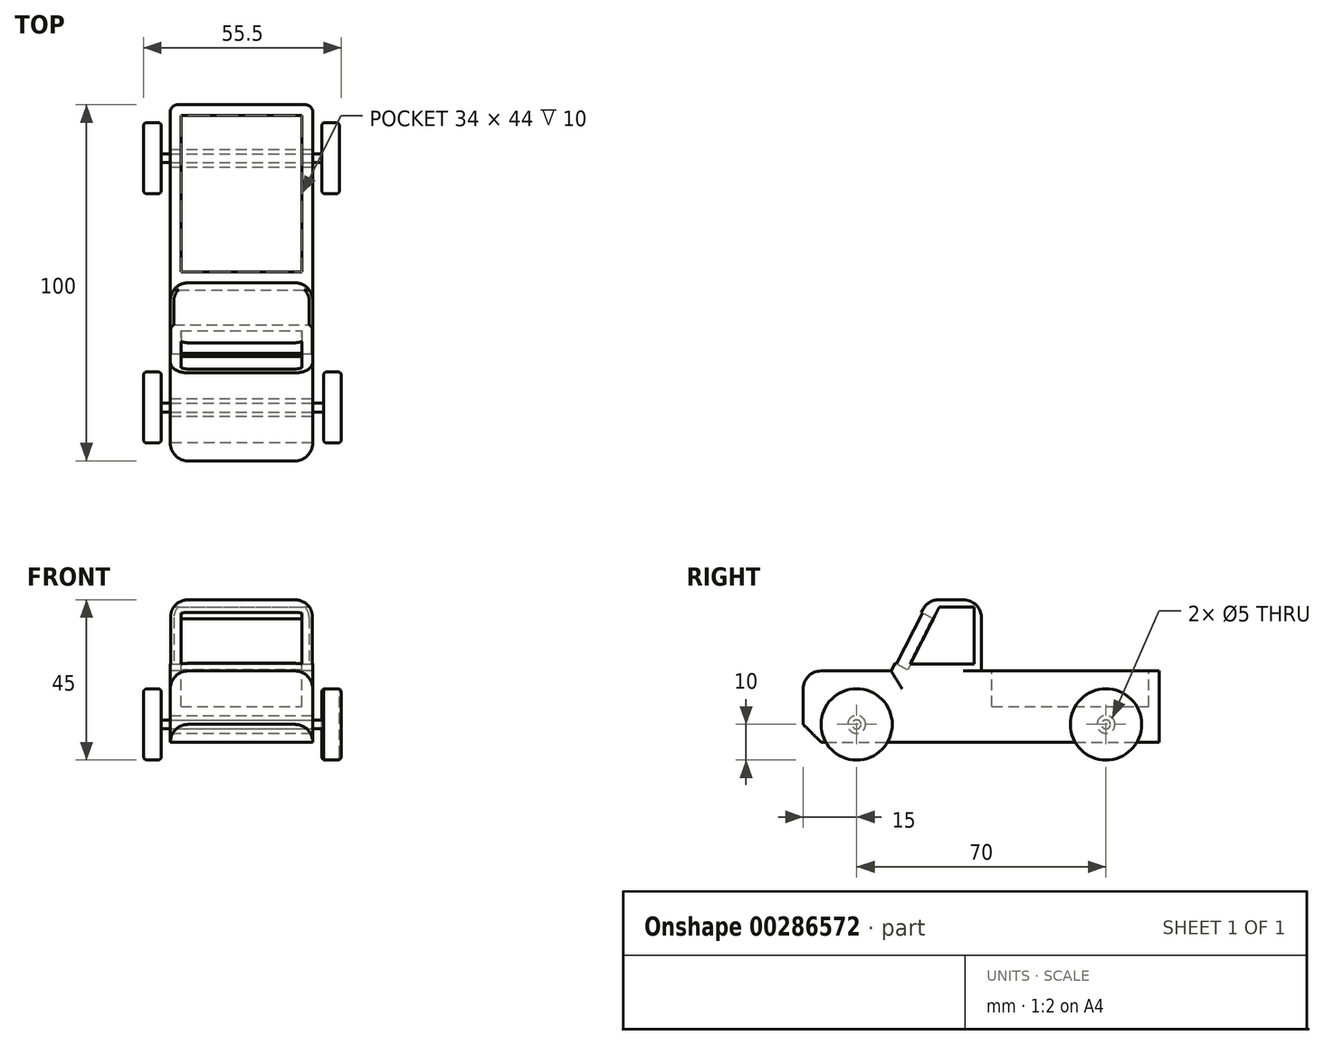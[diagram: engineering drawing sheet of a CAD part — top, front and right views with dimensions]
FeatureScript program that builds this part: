
annotation { "Feature Type Name" : "Feature", "Feature Type Description" : "" }
export const myFeature = defineFeature(function(context is Context, id is Id, definition is map)
    precondition{}
    {
        {
            var Q0;
            Q0=qCreatedBy(makeId("Right.planeOp"),FACE);
            var sketch = newSketch(context, id + "F0", { "sketchPlane" : qUnion([Q0])});
            skLineSegment(sketch, "E0.top", {"start": v(-50, -10) * mm, "end": v(50, -10) * mm});
            skLineSegment(sketch, "E0.left", {"start": v(-50, 10) * mm, "end": v(-50, -10) * mm});
            skLineSegment(sketch, "E0.right", {"start": v(50, 10) * mm, "end": v(50, -10) * mm});
            skPoint(sketch, "E0.middle", {"position": v(0, 0) * mm});
            skLineSegment(sketch, "E1", {"start": v(0, 10) * mm, "end": v(0, 30) * mm});
            skPoint(sketch, "E1.endSnap0", {"position": v(0, 10) * mm});
            skLineSegment(sketch, "E2", {"start": v(0, 30) * mm, "end": v(-15, 30) * mm});
            skPoint(sketch, "E3", {"position": v(-25.3, 10) * mm});
            skLineSegment(sketch, "E4", {"start": v(-15, 30) * mm, "end": v(-25.3, 10) * mm});
            skLineSegment(sketch, "E5", {"start": v(-50, 10) * mm, "end": v(-25.3, 10) * mm});
            skLineSegment(sketch, "E6", {"start": v(0, 10) * mm, "end": v(50, 10) * mm});
            skSolve(sketch);
        }
        {
            var Q0;
            Q0 = qSketchRegion(id + "F0", true);
            extrude(context, id + "F1", {"entities" : qUnion([Q0]), "endBound" : BoundingType.SYMMETRIC, "depth" : 40 * mm});
        }
        {
            var Q0;
            Q0=makeQuery(id+"F1.opExtrude","CAP_FACE",FACE,{"disambiguationData":[OSD([sQuery(id+"F0.wireOp",EDGE,"E0.bottom"),sQuery(id+"F0.wireOp",EDGE,"E0.top"),sQuery(id+"F0.wireOp",EDGE,"E0.left"),sQuery(id+"F0.wireOp",EDGE,"E0.right")])],"isStart":false});
            var sketch = newSketch(context, id + "F2", { "sketchPlane" : qUnion([Q0])});
            skCircle(sketch, "E7", {"center": v(-35, -5) * mm, "radius": 2.5 * mm});
            skCircle(sketch, "E8", {"center": v(165.27, -6.7) * mm, "radius": 18.84 * mm});
            skCircle(sketch, "E9", {"center": v(-35, -5) * mm, "radius": 1.25 * mm});
            skSolve(sketch);
        }
        {
            var Q0;
            Q0 = qSketchRegion(id + "F2", true);
            extrude(context, id + "F3", {"entities" : qUnion([Q0]), "operationType" : NewBodyOperationType.REMOVE, "endBound" : BoundingType.THROUGH_ALL, "oppositeDirection" : true, "depth" : 25 * mm});
        }
        {
            var Q0;
            Q0=makeQuery(id+"F1.opExtrude","CAP_FACE",FACE,{"disambiguationData":[OSD([sQuery(id+"F0.wireOp",EDGE,"E0.bottom"),sQuery(id+"F0.wireOp",EDGE,"E0.top"),sQuery(id+"F0.wireOp",EDGE,"E0.left"),sQuery(id+"F0.wireOp",EDGE,"E0.right")])],"isStart":false});
            var sketch = newSketch(context, id + "F4", { "sketchPlane" : qUnion([Q0])});
            skCircle(sketch, "E10", {"center": v(35, -5) * mm, "radius": 2.5 * mm});
            skCircle(sketch, "E11", {"center": v(35, -5) * mm, "radius": 1.25 * mm});
            skSolve(sketch);
        }
        {
            var Q0;
            Q0 = qSketchRegion(id + "F4", true);
            extrude(context, id + "F5", {"entities" : qUnion([Q0]), "operationType" : NewBodyOperationType.REMOVE, "endBound" : BoundingType.THROUGH_ALL, "oppositeDirection" : true, "depth" : 25 * mm});
        }
        {
            var Q0;
            Q0=makeQuery(id+"F1.opExtrude","SWEPT_FACE",FACE,{"disambiguationData":[OSD([sQuery(id+"F0.wireOp",EDGE,"E6")])]});
            var sketch = newSketch(context, id + "F6", { "sketchPlane" : qUnion([Q0])});
            skLineSegment(sketch, "E12.bottom", {"start": v(-17, 3) * mm, "end": v(17, 3) * mm});
            skLineSegment(sketch, "E12.top", {"start": v(-17, 47) * mm, "end": v(17, 47) * mm});
            skLineSegment(sketch, "E12.left", {"start": v(-17, 3) * mm, "end": v(-17, 47) * mm});
            skLineSegment(sketch, "E12.right", {"start": v(17, 3) * mm, "end": v(17, 47) * mm});
            skPoint(sketch, "E12.middle", {"position": v(0, 25) * mm});
            skSolve(sketch);
        }
        {
            var Q0;
            Q0=makeQuery(id+"F6.imprint","IMPRINT",FACE,{"disambiguationData":[TD([[makeQuery(id+"F6.imprint","IMPRINT",EDGE,{"derivedFrom":sQuery(id+"F6.wireOp",EDGE,"E12.bottom")}),1.0]])]});
            extrude(context, id + "F7", {"entities" : qUnion([Q0]), "operationType" : NewBodyOperationType.REMOVE, "oppositeDirection" : true, "depth" : 10 * mm});
        }
        {
            var Q0;
            Q0=makeQuery(id+"F3.boolean.opBoolean","SPLIT",FACE,{"disambiguationData":[TD([makeQuery(id+"F3.opExtrude","SWEPT_FACE",FACE,{"disambiguationData":[OSD([sQuery(id+"F2.wireOp",EDGE,"E9")])]})])],"derivedFrom":makeQuery(id+"F1.opExtrude","CAP_FACE",FACE,{"disambiguationData":[OSD([sQuery(id+"F0.wireOp",EDGE,"E0.top"),sQuery(id+"F0.wireOp",EDGE,"E0.left"),sQuery(id+"F0.wireOp",EDGE,"E0.right"),sQuery(id+"F0.wireOp",EDGE,"E1"),sQuery(id+"F0.wireOp",EDGE,"E2"),sQuery(id+"F0.wireOp",EDGE,"E4"),sQuery(id+"F0.wireOp",EDGE,"E5"),sQuery(id+"F0.wireOp",EDGE,"E6")])],"isStart":false})});
            extrude(context, id + "F8", {"entities" : qUnion([Q0]), "operationType" : NewBodyOperationType.ADD, "oppositeDirection" : true, "depth" : 42.5 * mm});
        }
        {
            var Q0;
            {var subQ0=sQuery(id+"F0.wireOp",EDGE,"E0.right");var subQ1=sQuery(id+"F0.wireOp",EDGE,"E0.left");var subQ2=sQuery(id+"F0.wireOp",EDGE,"E1");var subQ3=sQuery(id+"F0.wireOp",EDGE,"E0.top");var subQ4=sQuery(id+"F0.wireOp",EDGE,"E2");var subQ5=sQuery(id+"F0.wireOp",EDGE,"E4");var subQ6=sQuery(id+"F0.wireOp",EDGE,"E5");var subQ7=sQuery(id+"F0.wireOp",EDGE,"E6");Q0=makeQuery(id+"F5.boolean.opBoolean","SPLIT",FACE,{"disambiguationData":[TD([makeQuery(id+"F5.opExtrude","SWEPT_FACE",FACE,{"disambiguationData":[OSD([sQuery(id+"F4.wireOp",EDGE,"E11")])]})])],"derivedFrom":makeQuery(id+"F3.boolean.opBoolean","SPLIT",FACE,{"disambiguationData":[TD([makeQuery(id+"F1.opExtrude","SWEPT_FACE",FACE,{"disambiguationData":[OSD([subQ3])]})])],"derivedFrom":makeQuery(id+"F1.opExtrude","CAP_FACE",FACE,{"disambiguationData":[OSD([subQ3,subQ1,subQ0,subQ2,subQ4,subQ5,subQ6,subQ7])],"isStart":false})})});}
            extrude(context, id + "F9", {"entities" : qUnion([Q0]), "operationType" : NewBodyOperationType.ADD, "oppositeDirection" : true, "depth" : 42.5 * mm});
        }
        {
            var Q0;
            Q0=makeQuery(id+"F3.boolean.opBoolean","SPLIT",FACE,{"disambiguationData":[TD([makeQuery(id+"F3.opExtrude","SWEPT_FACE",FACE,{"disambiguationData":[OSD([sQuery(id+"F2.wireOp",EDGE,"E9")])]})])],"derivedFrom":makeQuery(id+"F1.opExtrude","CAP_FACE",FACE,{"disambiguationData":[OSD([sQuery(id+"F0.wireOp",EDGE,"E0.top"),sQuery(id+"F0.wireOp",EDGE,"E0.left"),sQuery(id+"F0.wireOp",EDGE,"E0.right"),sQuery(id+"F0.wireOp",EDGE,"E1"),sQuery(id+"F0.wireOp",EDGE,"E2"),sQuery(id+"F0.wireOp",EDGE,"E4"),sQuery(id+"F0.wireOp",EDGE,"E5"),sQuery(id+"F0.wireOp",EDGE,"E6")])],"isStart":false})});
            extrude(context, id + "F10", {"entities" : qUnion([Q0]), "operationType" : NewBodyOperationType.ADD, "depth" : 3 * mm});
        }
        {
            var Q0;
            {var subQ0=sQuery(id+"F0.wireOp",EDGE,"E0.right");var subQ1=sQuery(id+"F0.wireOp",EDGE,"E0.left");var subQ2=sQuery(id+"F0.wireOp",EDGE,"E1");var subQ3=sQuery(id+"F0.wireOp",EDGE,"E0.top");var subQ4=sQuery(id+"F0.wireOp",EDGE,"E2");var subQ5=sQuery(id+"F0.wireOp",EDGE,"E4");var subQ6=sQuery(id+"F0.wireOp",EDGE,"E5");var subQ7=sQuery(id+"F0.wireOp",EDGE,"E6");Q0=makeQuery(id+"F5.boolean.opBoolean","SPLIT",FACE,{"disambiguationData":[TD([makeQuery(id+"F5.opExtrude","SWEPT_FACE",FACE,{"disambiguationData":[OSD([sQuery(id+"F4.wireOp",EDGE,"E11")])]})])],"derivedFrom":makeQuery(id+"F3.boolean.opBoolean","SPLIT",FACE,{"disambiguationData":[TD([makeQuery(id+"F1.opExtrude","SWEPT_FACE",FACE,{"disambiguationData":[OSD([subQ3])]})])],"derivedFrom":makeQuery(id+"F1.opExtrude","CAP_FACE",FACE,{"disambiguationData":[OSD([subQ3,subQ1,subQ0,subQ2,subQ4,subQ5,subQ6,subQ7])],"isStart":false})})});}
            extrude(context, id + "F11", {"entities" : qUnion([Q0]), "operationType" : NewBodyOperationType.ADD, "depth" : 2.5 * mm});
        }
        {
            var Q0;
            Q0=makeQuery(id+"F10.opExtrude","CAP_FACE",FACE,{"disambiguationData":[OSD([sQuery(id+"F0.wireOp",EDGE,"E0.top"),sQuery(id+"F0.wireOp",EDGE,"E0.left"),sQuery(id+"F0.wireOp",EDGE,"E0.right"),sQuery(id+"F0.wireOp",EDGE,"E1"),sQuery(id+"F0.wireOp",EDGE,"E2"),sQuery(id+"F0.wireOp",EDGE,"E4"),sQuery(id+"F0.wireOp",EDGE,"E5"),sQuery(id+"F0.wireOp",EDGE,"E6")])],"isStart":false});
            var sketch = newSketch(context, id + "F12", { "sketchPlane" : qUnion([Q0])});
            skCircle(sketch, "E13", {"center": v(-35, -5) * mm, "radius": 10 * mm});
            skSolve(sketch);
        }
        {
            var Q0;
            Q0=makeQuery(id+"F12.imprint","IMPRINT",FACE,{"disambiguationData":[TD([[makeQuery(id+"F12.imprint","IMPRINT",EDGE,{"derivedFrom":sQuery(id+"F12.wireOp",EDGE,"E13")}),1.0]])]});
            extrude(context, id + "F13", {"entities" : qUnion([Q0]), "operationType" : NewBodyOperationType.ADD, "depth" : 5 * mm});
        }
        {
            var Q0;
            Q0=makeQuery(id+"F11.opExtrude","CAP_FACE",FACE,{"disambiguationData":[OSD([sQuery(id+"F0.wireOp",EDGE,"E0.top"),sQuery(id+"F0.wireOp",EDGE,"E0.left"),sQuery(id+"F0.wireOp",EDGE,"E0.right"),sQuery(id+"F0.wireOp",EDGE,"E1"),sQuery(id+"F0.wireOp",EDGE,"E2"),sQuery(id+"F0.wireOp",EDGE,"E4"),sQuery(id+"F0.wireOp",EDGE,"E5"),sQuery(id+"F0.wireOp",EDGE,"E6")])],"isStart":false});
            var sketch = newSketch(context, id + "F14", { "sketchPlane" : qUnion([Q0])});
            skCircle(sketch, "E14", {"center": v(35, -5) * mm, "radius": 10 * mm});
            skSolve(sketch);
        }
        {
            var Q0;
            Q0 = qSketchRegion(id + "F14", true);
            extrude(context, id + "F15", {"entities" : qUnion([Q0]), "operationType" : NewBodyOperationType.ADD, "depth" : 5 * mm});
        }
        {
            var Q0;
            Q0=makeQuery(id+"F13.opExtrude","SWEPT_BODY",BODY,{"disambiguationData":[OSD([sQuery(id+"F2.wireOp",EDGE,"E9"),sQuery(id+"F12.wireOp",EDGE,"E13")])]});
            deleteBodies(context, id + "F16", {"entities" : qUnion([Q0])});
        }
        {
            var Q0;
            Q0=makeQuery(id+"F10.opExtrude","CAP_FACE",FACE,{"disambiguationData":[OSD([sQuery(id+"F0.wireOp",EDGE,"E0.top"),sQuery(id+"F0.wireOp",EDGE,"E0.left"),sQuery(id+"F0.wireOp",EDGE,"E0.right"),sQuery(id+"F0.wireOp",EDGE,"E1"),sQuery(id+"F0.wireOp",EDGE,"E2"),sQuery(id+"F0.wireOp",EDGE,"E4"),sQuery(id+"F0.wireOp",EDGE,"E5"),sQuery(id+"F0.wireOp",EDGE,"E6")])],"isStart":false});
            var sketch = newSketch(context, id + "F17", { "sketchPlane" : qUnion([Q0])});
            skCircle(sketch, "E15", {"center": v(-35, -5) * mm, "radius": 10 * mm});
            skSolve(sketch);
        }
        {
            var Q0;
            Q0 = qSketchRegion(id + "F17", true);
            extrude(context, id + "F18", {"entities" : qUnion([Q0]), "operationType" : NewBodyOperationType.ADD, "depth" : 5 * mm});
        }
        {
            var Q0;
            Q0=makeQuery(id+"F9.opExtrude","CAP_FACE",FACE,{"disambiguationData":[OSD([sQuery(id+"F0.wireOp",EDGE,"E0.top"),sQuery(id+"F0.wireOp",EDGE,"E0.left"),sQuery(id+"F0.wireOp",EDGE,"E0.right"),sQuery(id+"F0.wireOp",EDGE,"E1"),sQuery(id+"F0.wireOp",EDGE,"E2"),sQuery(id+"F0.wireOp",EDGE,"E4"),sQuery(id+"F0.wireOp",EDGE,"E5"),sQuery(id+"F0.wireOp",EDGE,"E6")])],"isStart":false});
            var sketch = newSketch(context, id + "F19", { "sketchPlane" : qUnion([Q0])});
            skCircle(sketch, "E16", {"center": v(-35, -5) * mm, "radius": 10 * mm});
            skSolve(sketch);
        }
        {
            var Q0;
            Q0 = qSketchRegion(id + "F19", true);
            extrude(context, id + "F20", {"entities" : qUnion([Q0]), "operationType" : NewBodyOperationType.ADD, "depth" : 5 * mm});
        }
        {
            var Q0;
            Q0=makeQuery(id+"F8.opExtrude","CAP_FACE",FACE,{"disambiguationData":[OSD([sQuery(id+"F0.wireOp",EDGE,"E0.top"),sQuery(id+"F0.wireOp",EDGE,"E0.left"),sQuery(id+"F0.wireOp",EDGE,"E0.right"),sQuery(id+"F0.wireOp",EDGE,"E1"),sQuery(id+"F0.wireOp",EDGE,"E2"),sQuery(id+"F0.wireOp",EDGE,"E4"),sQuery(id+"F0.wireOp",EDGE,"E5"),sQuery(id+"F0.wireOp",EDGE,"E6")])],"isStart":false});
            var sketch = newSketch(context, id + "F21", { "sketchPlane" : qUnion([Q0])});
            skCircle(sketch, "E17", {"center": v(35, -5) * mm, "radius": 10 * mm});
            skSolve(sketch);
        }
        {
            var Q0;
            Q0 = qSketchRegion(id + "F21", true);
            extrude(context, id + "F22", {"entities" : qUnion([Q0]), "operationType" : NewBodyOperationType.ADD, "depth" : 5 * mm});
        }
        {
            var Q0;
            Q0=makeQuery(id+"F1.opExtrude","SWEPT_FACE",FACE,{"disambiguationData":[OSD([sQuery(id+"F0.wireOp",EDGE,"E4")])]});
            var sketch = newSketch(context, id + "F23", { "sketchPlane" : qUnion([Q0])});
            skLineSegment(sketch, "E18.bottom", {"start": v(17, 15.8) * mm, "end": v(-17, 15.8) * mm});
            skLineSegment(sketch, "E18.top", {"start": v(17, -0.3) * mm, "end": v(-17, -0.3) * mm});
            skLineSegment(sketch, "E18.left", {"start": v(17, 15.8) * mm, "end": v(17, -0.3) * mm});
            skLineSegment(sketch, "E18.right", {"start": v(-17, 15.8) * mm, "end": v(-17, -0.3) * mm});
            skPoint(sketch, "E18.middle", {"position": v(0, 7.75) * mm});
            skSolve(sketch);
        }
        {
            var Q0;
            Q0 = qSketchRegion(id + "F23", true);
            extrude(context, id + "F24", {"entities" : qUnion([Q0]), "operationType" : NewBodyOperationType.REMOVE, "oppositeDirection" : true, "depth" : 4 * mm});
        }
        {
            var Q0;
            {var subQ0=sQuery(id+"F0.wireOp",EDGE,"E0.right");var subQ2=sQuery(id+"F0.wireOp",EDGE,"E0.left");var subQ4=sQuery(id+"F0.wireOp",EDGE,"E1");var subQ7=sQuery(id+"F0.wireOp",EDGE,"E0.top");var subQ8=makeQuery(id+"F1.opExtrude","SWEPT_FACE",FACE,{"disambiguationData":[OSD([subQ7])]});var subQ9=sQuery(id+"F0.wireOp",EDGE,"E2");var subQ11=sQuery(id+"F0.wireOp",EDGE,"E4");var subQ13=sQuery(id+"F0.wireOp",EDGE,"E5");var subQ15=sQuery(id+"F0.wireOp",EDGE,"E6");Q0=makeQuery(id+"F5.boolean.opBoolean","SPLIT",FACE,{"disambiguationData":[TD([subQ8])],"derivedFrom":makeQuery(id+"F3.boolean.opBoolean","SPLIT",FACE,{"disambiguationData":[TD([subQ8])],"derivedFrom":makeQuery(id+"F1.opExtrude","CAP_FACE",FACE,{"disambiguationData":[OSD([subQ7,subQ2,subQ0,subQ4,subQ9,subQ11,subQ13,subQ15])],"isStart":false})})});}
            var sketch = newSketch(context, id + "F25", { "sketchPlane" : qUnion([Q0])});
            skLineSegment(sketch, "E19", {"start": v(-19.96, 12) * mm, "end": v(-2, 12) * mm});
            skLineSegment(sketch, "E20", {"start": v(-2, 12) * mm, "end": v(-2, 28) * mm});
            skLineSegment(sketch, "E21", {"start": v(-2, 28) * mm, "end": v(-11.78, 28) * mm});
            skLineSegment(sketch, "E22", {"start": v(-11.78, 28) * mm, "end": v(-19.96, 12) * mm});
            skSolve(sketch);
        }
        {
            var Q0;
            Q0 = qSketchRegion(id + "F25", true);
            extrude(context, id + "F26", {"entities" : qUnion([Q0]), "operationType" : NewBodyOperationType.REMOVE, "endBound" : BoundingType.THROUGH_ALL, "oppositeDirection" : true, "depth" : 25 * mm});
        }
        {
            var Q0;
            Q0=makeQuery(id+"F1.opExtrude","SWEPT_EDGE",EDGE,{"disambiguationData":[OSD([sQuery(id+"F0.wireOp",EDGE,"E0.left"),sQuery(id+"F0.wireOp",EDGE,"E5")])]});
            fillet(context, id + "F27", {"entities" : qUnion([Q0]), "radius" : 5 * mm, "tangentPropagation" : true, "allowEdgeOverflow" : false});
        }
        {
            var Q0;
            Q0=makeQuery(id+"F1.opExtrude","SWEPT_EDGE",EDGE,{"disambiguationData":[OSD([sQuery(id+"F0.wireOp",EDGE,"E2"),sQuery(id+"F0.wireOp",EDGE,"E4")])]});
            fillet(context, id + "F28", {"entities" : qUnion([Q0]), "radius" : 5 * mm, "tangentPropagation" : true, "allowEdgeOverflow" : false});
        }
        {
            var Q0;
            Q0=makeQuery(id+"F1.opExtrude","SWEPT_EDGE",EDGE,{"disambiguationData":[OSD([sQuery(id+"F0.wireOp",EDGE,"E1"),sQuery(id+"F0.wireOp",EDGE,"E2")])]});
            fillet(context, id + "F29", {"entities" : qUnion([Q0]), "radius" : 5 * mm, "tangentPropagation" : true, "allowEdgeOverflow" : false});
        }
        {
            var Q0;
            Q0=makeQuery(id+"F1.opExtrude","SWEPT_EDGE",EDGE,{"disambiguationData":[OSD([sQuery(id+"F0.wireOp",EDGE,"E0.top"),sQuery(id+"F0.wireOp",EDGE,"E0.left")])]});
            chamfer(context, id + "F30", {"entities" : qUnion([Q0]), "width" : 5 * mm, "tangentPropagation" : true});
        }
        {
            var Q0;
            {var subQ0=sQuery(id+"F0.wireOp",EDGE,"E0.right");var subQ2=sQuery(id+"F0.wireOp",EDGE,"E0.left");var subQ4=sQuery(id+"F0.wireOp",EDGE,"E1");var subQ7=sQuery(id+"F0.wireOp",EDGE,"E0.top");var subQ8=makeQuery(id+"F1.opExtrude","SWEPT_FACE",FACE,{"disambiguationData":[OSD([subQ7])]});var subQ9=sQuery(id+"F0.wireOp",EDGE,"E2");var subQ11=sQuery(id+"F0.wireOp",EDGE,"E4");var subQ13=sQuery(id+"F0.wireOp",EDGE,"E5");var subQ15=sQuery(id+"F0.wireOp",EDGE,"E6");Q0=makeQuery(id+"F27.opFillet","BLEND_EDGE",EDGE,{"blendedFrom":[makeQuery(id+"F1.opExtrude","SWEPT_EDGE",EDGE,{"disambiguationData":[OSD([subQ2,subQ13])]}),makeQuery(id+"F5.boolean.opBoolean","SPLIT",FACE,{"disambiguationData":[TD([subQ8])],"derivedFrom":makeQuery(id+"F3.boolean.opBoolean","SPLIT",FACE,{"disambiguationData":[TD([subQ8])],"derivedFrom":makeQuery(id+"F1.opExtrude","CAP_FACE",FACE,{"disambiguationData":[OSD([subQ7,subQ2,subQ0,subQ4,subQ9,subQ11,subQ13,subQ15])],"isStart":false})})})],"blendedInto":[makeQuery(id+"F5.boolean.opBoolean","SPLIT",FACE,{"disambiguationData":[TD([subQ8])],"derivedFrom":makeQuery(id+"F3.boolean.opBoolean","SPLIT",FACE,{"disambiguationData":[TD([subQ8])],"derivedFrom":makeQuery(id+"F1.opExtrude","CAP_FACE",FACE,{"disambiguationData":[OSD([subQ7,subQ2,subQ0,subQ4,subQ9,subQ11,subQ13,subQ15])],"isStart":false})})})]});}
            fillet(context, id + "F31", {"entities" : qUnion([Q0]), "radius" : 5 * mm, "tangentPropagation" : true, "allowEdgeOverflow" : false});
        }
        {
            var Q0;
            {var subQ0=sQuery(id+"F0.wireOp",EDGE,"E0.right");var subQ2=sQuery(id+"F0.wireOp",EDGE,"E0.left");var subQ4=sQuery(id+"F0.wireOp",EDGE,"E1");var subQ7=sQuery(id+"F0.wireOp",EDGE,"E0.top");var subQ8=makeQuery(id+"F1.opExtrude","SWEPT_FACE",FACE,{"disambiguationData":[OSD([subQ7])]});var subQ9=sQuery(id+"F0.wireOp",EDGE,"E2");var subQ11=sQuery(id+"F0.wireOp",EDGE,"E4");var subQ13=sQuery(id+"F0.wireOp",EDGE,"E5");var subQ15=sQuery(id+"F0.wireOp",EDGE,"E6");Q0=makeQuery(id+"F27.opFillet","BLEND_EDGE",EDGE,{"blendedFrom":[makeQuery(id+"F1.opExtrude","SWEPT_EDGE",EDGE,{"disambiguationData":[OSD([subQ2,subQ13])]}),makeQuery(id+"F5.boolean.opBoolean","SPLIT",FACE,{"disambiguationData":[TD([subQ8])],"derivedFrom":makeQuery(id+"F3.boolean.opBoolean","SPLIT",FACE,{"disambiguationData":[TD([subQ8])],"derivedFrom":makeQuery(id+"F1.opExtrude","CAP_FACE",FACE,{"disambiguationData":[OSD([subQ7,subQ2,subQ0,subQ4,subQ9,subQ11,subQ13,subQ15])],"isStart":true})})})],"blendedInto":[makeQuery(id+"F5.boolean.opBoolean","SPLIT",FACE,{"disambiguationData":[TD([subQ8])],"derivedFrom":makeQuery(id+"F3.boolean.opBoolean","SPLIT",FACE,{"disambiguationData":[TD([subQ8])],"derivedFrom":makeQuery(id+"F1.opExtrude","CAP_FACE",FACE,{"disambiguationData":[OSD([subQ7,subQ2,subQ0,subQ4,subQ9,subQ11,subQ13,subQ15])],"isStart":true})})})]});}
            fillet(context, id + "F32", {"entities" : qUnion([Q0]), "radius" : 5 * mm, "tangentPropagation" : true, "allowEdgeOverflow" : false});
        }
        {
            var Q0;
            Q0=makeQuery(id+"F1.opExtrude","CAP_EDGE",EDGE,{"disambiguationData":[OSD([sQuery(id+"F0.wireOp",EDGE,"E0.right")])],"isStart":true});
            fillet(context, id + "F33", {"entities" : qUnion([Q0]), "radius" : 2 * mm, "tangentPropagation" : true, "allowEdgeOverflow" : false});
        }
        {
            var Q0;
            Q0=makeQuery(id+"F1.opExtrude","CAP_EDGE",EDGE,{"disambiguationData":[OSD([sQuery(id+"F0.wireOp",EDGE,"E0.right")])],"isStart":false});
            fillet(context, id + "F34", {"entities" : qUnion([Q0]), "radius" : 2 * mm, "tangentPropagation" : true, "allowEdgeOverflow" : false});
        }
        {
            var Q0;
            Q0=makeQuery(id+"F18.opExtrude","CAP_EDGE",EDGE,{"disambiguationData":[OSD([sQuery(id+"F17.wireOp",EDGE,"E15")])],"isStart":true});
            fillet(context, id + "F35", {"entities" : qUnion([Q0]), "radius" : 1 * mm, "tangentPropagation" : true, "allowEdgeOverflow" : false});
        }
        {
            var Q0;
            Q0=makeQuery(id+"F18.opExtrude","CAP_EDGE",EDGE,{"disambiguationData":[OSD([sQuery(id+"F17.wireOp",EDGE,"E15")])],"isStart":false});
            fillet(context, id + "F36", {"entities" : qUnion([Q0]), "radius" : 1 * mm, "tangentPropagation" : true, "allowEdgeOverflow" : false});
        }
        {
            var Q0;
            Q0=makeQuery(id+"F15.opExtrude","CAP_EDGE",EDGE,{"disambiguationData":[OSD([sQuery(id+"F14.wireOp",EDGE,"E14")])],"isStart":true});
            fillet(context, id + "F37", {"entities" : qUnion([Q0]), "radius" : 1 * mm, "tangentPropagation" : true, "allowEdgeOverflow" : false});
        }
        {
            var Q0;
            Q0=makeQuery(id+"F15.opExtrude","CAP_EDGE",EDGE,{"disambiguationData":[OSD([sQuery(id+"F14.wireOp",EDGE,"E14")])],"isStart":false});
            fillet(context, id + "F38", {"entities" : qUnion([Q0]), "radius" : 1 * mm, "tangentPropagation" : true, "allowEdgeOverflow" : false});
        }
        {
            var Q0;
            Q0=makeQuery(id+"F20.opExtrude","CAP_EDGE",EDGE,{"disambiguationData":[OSD([sQuery(id+"F19.wireOp",EDGE,"E16")])],"isStart":true});
            fillet(context, id + "F39", {"entities" : qUnion([Q0]), "radius" : 1 * mm, "tangentPropagation" : true, "allowEdgeOverflow" : false});
        }
        {
            var Q0;
            Q0=makeQuery(id+"F20.opExtrude","CAP_EDGE",EDGE,{"disambiguationData":[OSD([sQuery(id+"F19.wireOp",EDGE,"E16")])],"isStart":false});
            fillet(context, id + "F40", {"entities" : qUnion([Q0]), "radius" : 1 * mm, "tangentPropagation" : true, "allowEdgeOverflow" : false});
        }
        {
            var Q0;
            Q0=makeQuery(id+"F22.opExtrude","CAP_EDGE",EDGE,{"disambiguationData":[OSD([sQuery(id+"F21.wireOp",EDGE,"E17")])],"isStart":true});
            fillet(context, id + "F41", {"entities" : qUnion([Q0]), "radius" : 1 * mm, "tangentPropagation" : true, "allowEdgeOverflow" : false});
        }
        {
            var Q0;
            Q0=makeQuery(id+"F22.opExtrude","CAP_EDGE",EDGE,{"disambiguationData":[OSD([sQuery(id+"F21.wireOp",EDGE,"E17")])],"isStart":false});
            fillet(context, id + "F42", {"entities" : qUnion([Q0]), "radius" : 1 * mm, "tangentPropagation" : true, "allowEdgeOverflow" : false});
        }
        {
            var Q0;
            Q0=makeQuery(id+"F1.opExtrude","CAP_EDGE",EDGE,{"disambiguationData":[OSD([sQuery(id+"F0.wireOp",EDGE,"E1")])],"isStart":true});
            fillet(context, id + "F43", {"entities" : qUnion([Q0]), "radius" : 5 * mm, "tangentPropagation" : true, "allowEdgeOverflow" : false});
        }
        {
            var Q0;
            Q0=makeQuery(id+"F1.opExtrude","CAP_EDGE",EDGE,{"disambiguationData":[OSD([sQuery(id+"F0.wireOp",EDGE,"E1")])],"isStart":false});
            fillet(context, id + "F44", {"entities" : qUnion([Q0]), "radius" : 5 * mm, "tangentPropagation" : true, "allowEdgeOverflow" : false});
        }
    });
